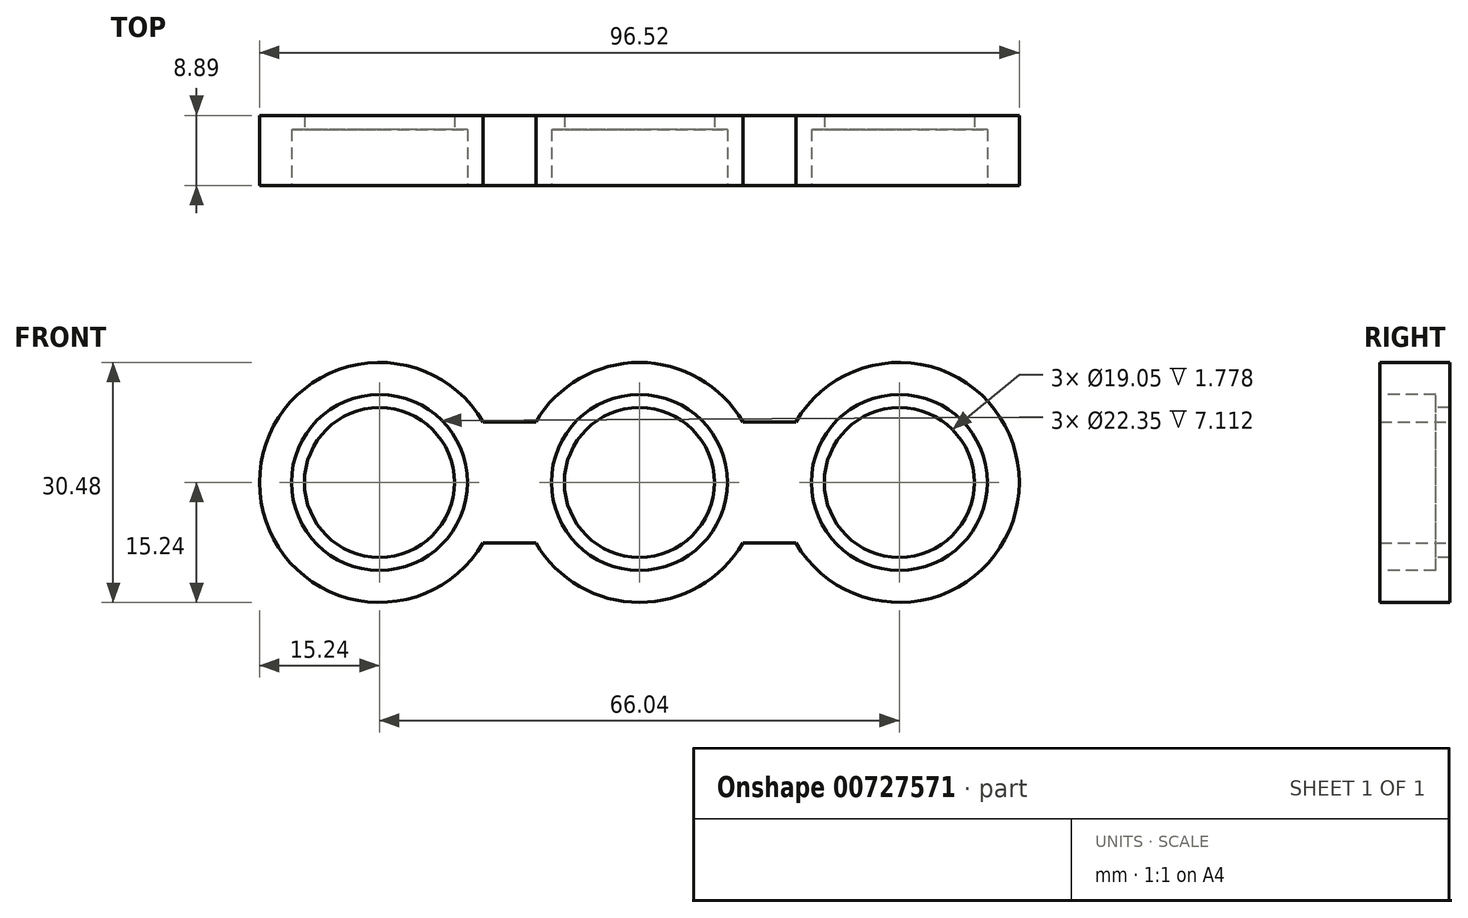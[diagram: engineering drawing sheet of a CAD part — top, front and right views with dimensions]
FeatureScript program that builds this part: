
annotation { "Feature Type Name" : "Feature", "Feature Type Description" : "" }
export const myFeature = defineFeature(function(context is Context, id is Id, definition is map)
    precondition{}
    {
        {
            var Q0;
            Q0=qCreatedBy(makeId("Front.planeOp"),FACE);
            var sketch = newSketch(context, id + "F0", { "sketchPlane" : qUnion([Q0])});
            skLineSegment(sketch, "E0.bottom", {"start": v(33.02, -7.7) * mm, "end": v(-33.02, -7.7) * mm});
            skLineSegment(sketch, "E0.top", {"start": v(33.02, 7.7) * mm, "end": v(-33.02, 7.7) * mm});
            skLineSegment(sketch, "E0.left", {"start": v(33.02, -7.7) * mm, "end": v(33.02, 7.7) * mm});
            skLineSegment(sketch, "E0.right", {"start": v(-33.02, -7.7) * mm, "end": v(-33.02, 7.7) * mm});
            skPoint(sketch, "E0.middle", {"position": v(0, 0) * mm});
            skCircle(sketch, "E1", {"center": v(0, 0) * mm, "radius": 15.24 * mm});
            skCircle(sketch, "E2", {"center": v(-33.02, 0) * mm, "radius": 15.24 * mm});
            skCircle(sketch, "E3", {"center": v(33.02, 0) * mm, "radius": 15.24 * mm});
            skSolve(sketch);
        }
        {
            var Q0;
            Q0 = qSketchRegion(id + "F0", true);
            extrude(context, id + "F1", {"entities" : qUnion([Q0]), "depth" : 8.9 * mm, "offsetDistance" : 25.4 * mm});
        }
        {
            var Q0;
            Q0=makeQuery(id+"F1.opExtrude","CAP_FACE",FACE,{"disambiguationData":[OSD([sQuery(id+"F0.wireOp",EDGE,"E0.bottom"),sQuery(id+"F0.wireOp",EDGE,"E0.top"),sQuery(id+"F0.wireOp",EDGE,"E1"),sQuery(id+"F0.wireOp",EDGE,"E2"),sQuery(id+"F0.wireOp",EDGE,"E3")])],"isStart":false});
            var sketch = newSketch(context, id + "F2", { "sketchPlane" : qUnion([Q0])});
            skCircle(sketch, "E4", {"center": v(0, 0) * mm, "radius": 9.53 * mm});
            skCircle(sketch, "E5", {"center": v(33.02, 0) * mm, "radius": 9.53 * mm});
            skCircle(sketch, "E6", {"center": v(-33.02, 0) * mm, "radius": 9.53 * mm});
            skSolve(sketch);
        }
        {
            var Q0;
            Q0=makeQuery(id+"F2.imprint","IMPRINT",FACE,{"disambiguationData":[TD([[makeQuery(id+"F2.imprint","IMPRINT",EDGE,{"derivedFrom":sQuery(id+"F2.wireOp",EDGE,"E4")}),1.0]])]});
            var Q1;
            Q1=makeQuery(id+"F2.imprint","IMPRINT",FACE,{"disambiguationData":[TD([[makeQuery(id+"F2.imprint","IMPRINT",EDGE,{"derivedFrom":sQuery(id+"F2.wireOp",EDGE,"E5")}),1.0]])]});
            var Q2;
            Q2=makeQuery(id+"F2.imprint","IMPRINT",FACE,{"disambiguationData":[TD([[makeQuery(id+"F2.imprint","IMPRINT",EDGE,{"derivedFrom":sQuery(id+"F2.wireOp",EDGE,"E6")}),1.0]])]});
            extrude(context, id + "F3", {"entities" : qUnion([Q0, Q1, Q2]), "operationType" : NewBodyOperationType.REMOVE, "oppositeDirection" : true, "depth" : 9.14 * mm, "offsetDistance" : 25.4 * mm});
        }
        {
            var Q0;
            Q0=makeQuery(id+"F1.opExtrude","CAP_FACE",FACE,{"disambiguationData":[OSD([sQuery(id+"F0.wireOp",EDGE,"E0.bottom"),sQuery(id+"F0.wireOp",EDGE,"E0.top"),sQuery(id+"F0.wireOp",EDGE,"E1"),sQuery(id+"F0.wireOp",EDGE,"E2"),sQuery(id+"F0.wireOp",EDGE,"E3")])],"isStart":false});
            var sketch = newSketch(context, id + "F4", { "sketchPlane" : qUnion([Q0])});
            skCircle(sketch, "E7", {"center": v(0, 0) * mm, "radius": 11.18 * mm});
            skCircle(sketch, "E8", {"center": v(-33.02, 0) * mm, "radius": 11.18 * mm});
            skCircle(sketch, "E9", {"center": v(33.02, 0) * mm, "radius": 11.18 * mm});
            skSolve(sketch);
        }
        {
            var Q0;
            Q0 = qSketchRegion(id + "F4", true);
            extrude(context, id + "F5", {"entities" : qUnion([Q0]), "operationType" : NewBodyOperationType.REMOVE, "oppositeDirection" : true, "depth" : 7.11 * mm, "offsetDistance" : 25.4 * mm});
        }
    });
